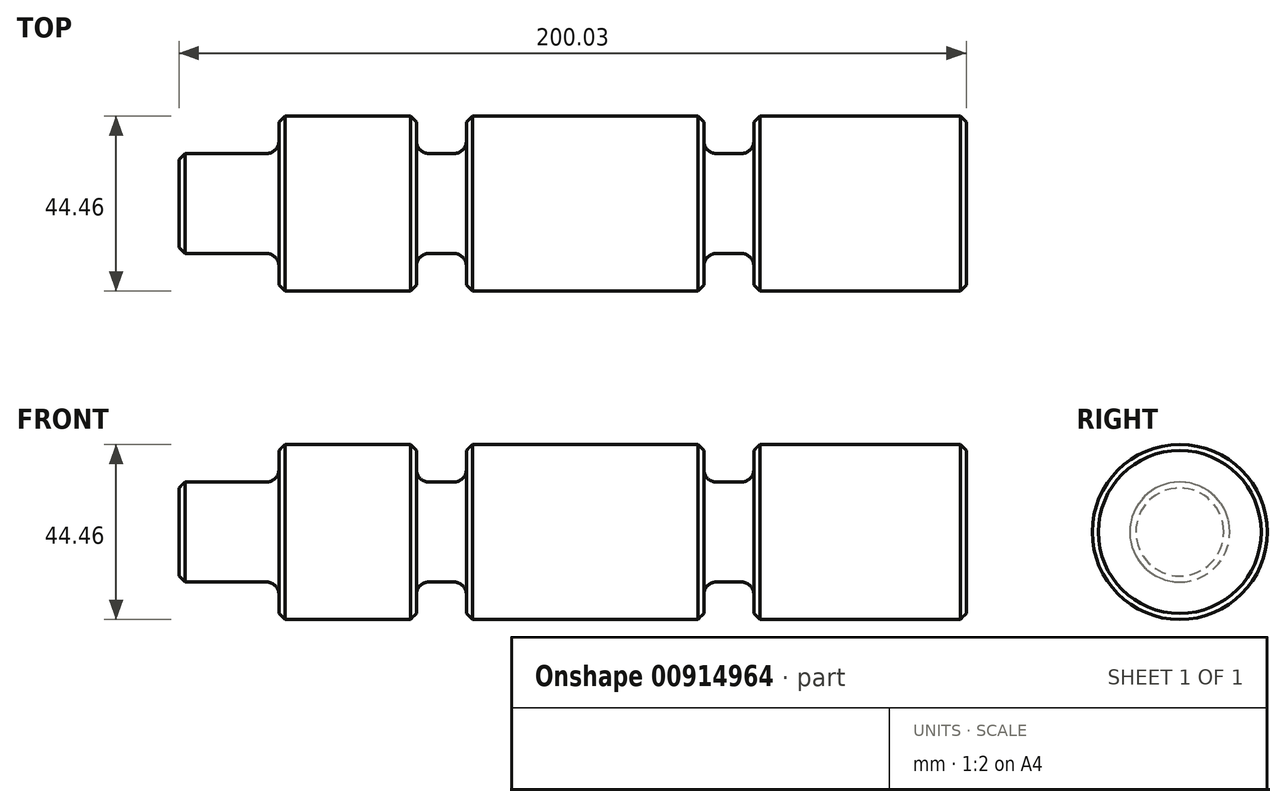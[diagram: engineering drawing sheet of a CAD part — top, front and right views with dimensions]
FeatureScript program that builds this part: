
annotation { "Feature Type Name" : "Feature", "Feature Type Description" : "" }
export const myFeature = defineFeature(function(context is Context, id is Id, definition is map)
    precondition{}
    {
        {
            var Q0;
            Q0=qCreatedBy(makeId("Front.planeOp"),FACE);
            var sketch = newSketch(context, id + "F0", { "sketchPlane" : qUnion([Q0])});
            skLineSegment(sketch, "E0", {"start": v(98.42, 0) * mm, "end": v(-101.6, 0) * mm});
            skLineSegment(sketch, "E1", {"start": v(-101.6, 0) * mm, "end": v(-101.6, 12.7) * mm});
            skLineSegment(sketch, "E2", {"start": v(-101.6, 12.7) * mm, "end": v(-76.2, 12.7) * mm});
            skLineSegment(sketch, "E3", {"start": v(-76.2, 12.7) * mm, "end": v(-76.2, 22.22) * mm});
            skLineSegment(sketch, "E4", {"start": v(-76.2, 22.22) * mm, "end": v(-41.28, 22.22) * mm});
            skLineSegment(sketch, "E5", {"start": v(-41.28, 22.22) * mm, "end": v(-41.28, 12.7) * mm});
            skLineSegment(sketch, "E6", {"start": v(-41.28, 12.7) * mm, "end": v(-28.58, 12.7) * mm});
            skLineSegment(sketch, "E7", {"start": v(-28.58, 12.7) * mm, "end": v(-28.58, 22.22) * mm});
            skLineSegment(sketch, "E8", {"start": v(-28.58, 22.22) * mm, "end": v(31.75, 22.22) * mm});
            skLineSegment(sketch, "E9", {"start": v(31.75, 22.22) * mm, "end": v(31.75, 12.7) * mm});
            skLineSegment(sketch, "E10", {"start": v(31.75, 12.7) * mm, "end": v(44.45, 12.7) * mm});
            skLineSegment(sketch, "E11", {"start": v(44.45, 12.7) * mm, "end": v(44.45, 22.22) * mm});
            skLineSegment(sketch, "E12", {"start": v(44.45, 22.22) * mm, "end": v(98.42, 22.22) * mm});
            skLineSegment(sketch, "E13", {"start": v(98.42, 22.22) * mm, "end": v(98.42, 0) * mm});
            skLineSegment(sketch, "E14", {"start": v(-115.42, 0) * mm, "end": v(112.1, 0) * mm, "construction": true});
            skSolve(sketch);
        }
        {
            var Q0;
            Q0 = qSketchRegion(id + "F0", true);
            var Q1;
            Q1=sQuery(id+"F0.wireOp",EDGE,"E14");
            revolve(context, id + "F1", {"surfaceOperationType" : NewSurfaceOperationType.NEW, "entities" : qUnion([Q0]), "axis" : qUnion([Q1]), "revolveType" : RevolveType.FULL});
        }
        {
            var Q0;
            Q0=makeQuery(id+"F1.opRevolve","SWEPT_EDGE",EDGE,{"disambiguationData":[OSD([sQuery(id+"F0.wireOp",EDGE,"E1"),sQuery(id+"F0.wireOp",EDGE,"E2")])]});
            var Q1;
            Q1=makeQuery(id+"F1.opRevolve","SWEPT_EDGE",EDGE,{"disambiguationData":[OSD([sQuery(id+"F0.wireOp",EDGE,"E3"),sQuery(id+"F0.wireOp",EDGE,"E4")])]});
            var Q2;
            Q2=makeQuery(id+"F1.opRevolve","SWEPT_EDGE",EDGE,{"disambiguationData":[OSD([sQuery(id+"F0.wireOp",EDGE,"E4"),sQuery(id+"F0.wireOp",EDGE,"E5")])]});
            var Q3;
            Q3=makeQuery(id+"F1.opRevolve","SWEPT_EDGE",EDGE,{"disambiguationData":[OSD([sQuery(id+"F0.wireOp",EDGE,"E7"),sQuery(id+"F0.wireOp",EDGE,"E8")])]});
            var Q4;
            Q4=makeQuery(id+"F1.opRevolve","SWEPT_EDGE",EDGE,{"disambiguationData":[OSD([sQuery(id+"F0.wireOp",EDGE,"E8"),sQuery(id+"F0.wireOp",EDGE,"E9")])]});
            var Q5;
            Q5=makeQuery(id+"F1.opRevolve","SWEPT_EDGE",EDGE,{"disambiguationData":[OSD([sQuery(id+"F0.wireOp",EDGE,"E11"),sQuery(id+"F0.wireOp",EDGE,"E12")])]});
            var Q6;
            Q6=makeQuery(id+"F1.opRevolve","SWEPT_EDGE",EDGE,{"disambiguationData":[OSD([sQuery(id+"F0.wireOp",EDGE,"E12"),sQuery(id+"F0.wireOp",EDGE,"E13")])]});
            chamfer(context, id + "F2", {"entities" : qUnion([Q0, Q1, Q2, Q3, Q4, Q5, Q6]), "width" : 1.52 * mm, "tangentPropagation" : true});
        }
        {
            var Q0;
            Q0=makeQuery(id+"F1.opRevolve","SWEPT_EDGE",EDGE,{"disambiguationData":[OSD([sQuery(id+"F0.wireOp",EDGE,"E2"),sQuery(id+"F0.wireOp",EDGE,"E3")])]});
            var Q1;
            Q1=makeQuery(id+"F1.opRevolve","SWEPT_EDGE",EDGE,{"disambiguationData":[OSD([sQuery(id+"F0.wireOp",EDGE,"E6"),sQuery(id+"F0.wireOp",EDGE,"E7")])]});
            var Q2;
            Q2=makeQuery(id+"F1.opRevolve","SWEPT_EDGE",EDGE,{"disambiguationData":[OSD([sQuery(id+"F0.wireOp",EDGE,"E10"),sQuery(id+"F0.wireOp",EDGE,"E11")])]});
            var Q3;
            Q3=makeQuery(id+"F1.opRevolve","SWEPT_EDGE",EDGE,{"disambiguationData":[OSD([sQuery(id+"F0.wireOp",EDGE,"E5"),sQuery(id+"F0.wireOp",EDGE,"E6")])]});
            var Q4;
            Q4=makeQuery(id+"F1.opRevolve","SWEPT_EDGE",EDGE,{"disambiguationData":[OSD([sQuery(id+"F0.wireOp",EDGE,"E9"),sQuery(id+"F0.wireOp",EDGE,"E10")])]});
            fillet(context, id + "F3", {"entities" : qUnion([Q0, Q1, Q2, Q3, Q4]), "radius" : 3.17 * mm, "tangentPropagation" : true, "allowEdgeOverflow" : false});
        }
    });
